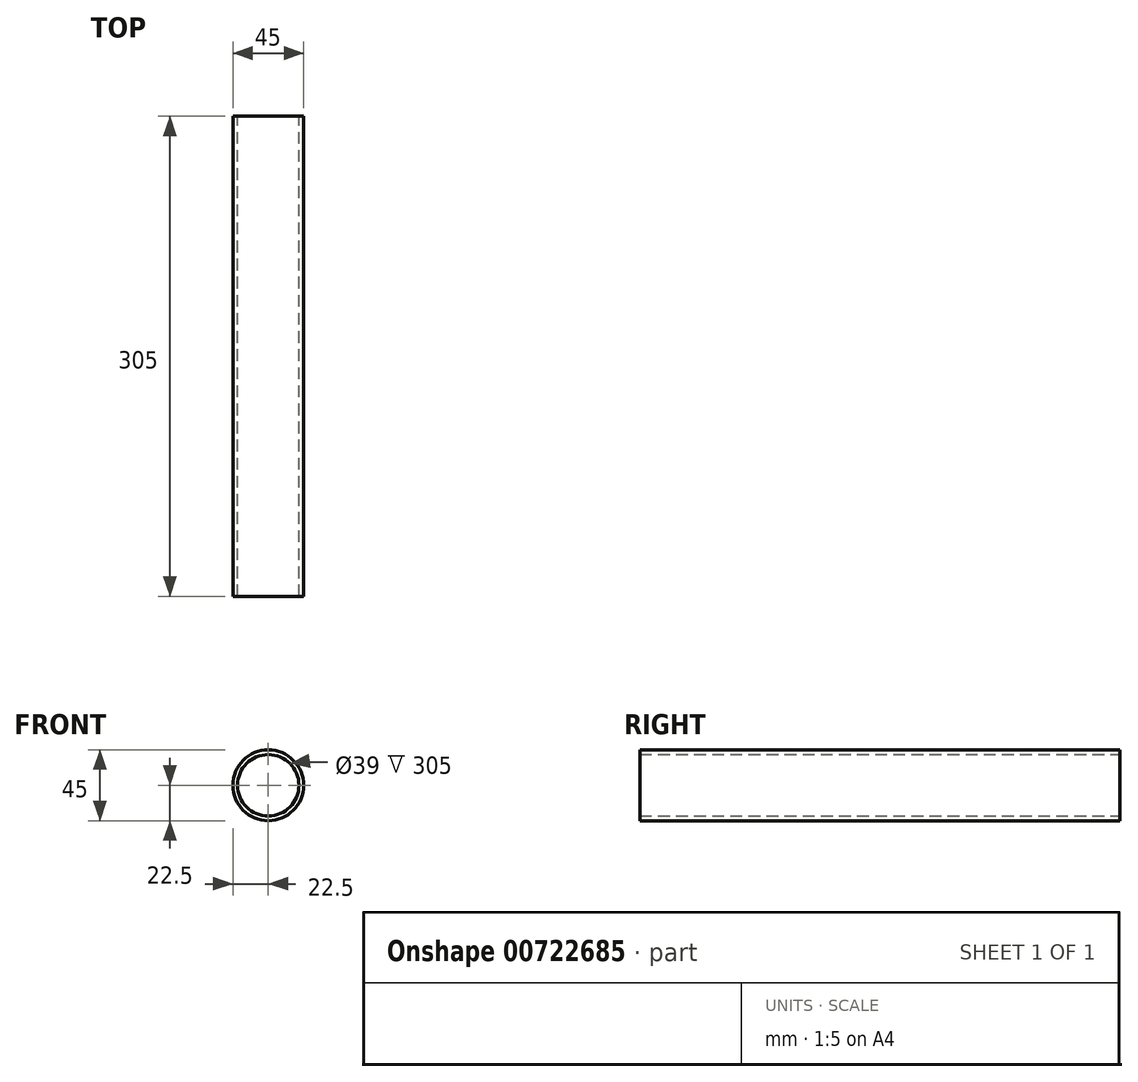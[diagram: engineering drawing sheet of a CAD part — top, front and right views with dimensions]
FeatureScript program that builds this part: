
annotation { "Feature Type Name" : "Feature", "Feature Type Description" : "" }
export const myFeature = defineFeature(function(context is Context, id is Id, definition is map)
    precondition{}
    {
        {
            var Q0;
            Q0=qCreatedBy(makeId("Front.planeOp"),FACE);
            var sketch = newSketch(context, id + "F0", { "sketchPlane" : qUnion([Q0])});
            skCircle(sketch, "E0", {"center": v(0, 0) * mm, "radius": 22.5 * mm});
            skCircle(sketch, "E1", {"center": v(0, 0) * mm, "radius": 19.5 * mm});
            skSolve(sketch);
        }
        {
            var Q0;
            Q0 = qSketchRegion(id + "F0", true);
            extrude(context, id + "F1", {"entities" : qUnion([Q0]), "depth" : 305 * mm, "offsetDistance" : 25 * mm, "symmetric" : true});
        }
    });
